# Revit family: PRD_AR_TltRllHldrs_STRATOSJumboRollHolder_STRX670
name_source: partatom
category: Specialty Equipment
revit_build: Autodesk Revit 2018 (Build: 20190510_1515(x64)
units: mm (PartAtom-declared; Revit-internal decimal feet)

## family parameters
Cut with Voids When Loaded = No
Host = Face
OmniClass Number = 23.40.20.21.17
OmniClass Title = Paper Towel Dispensers, Disposal Units
Part Type = Normal
Room Calculation Point = No
Round Connector Dimension = Use Diameter
Shared = No

## types (1)
- STRX670
    AssetType = Fixed
    BIMObjectName = PRD_AR_ToiletRollHolders_STRATOSJumboRollHolder_STRX670
    Category = Pr_40_20_76_88, Toilet roll holders
    Default Elevation = 850 mm  [stored 2.78871 ft]
    Description = Jumbo roll holder for wall mounting, stainless steel, surface satin finished, front with InoxPlus surface refinement for the reduction of finger marks and better cleaning characteristics (easy to clean), material thickness 1.5 mm, closed casing with curved front, paper withdrawal over two tear-off edges, cylinder lock with KWC standard key, for 1 roll with max. Ø 295 mm, includes stainless steel screws and dowels.
    DurationUnit = year
    Features = stainless steel, surface satin finished
    FillingQuantity = 1
    FillingQuantityUom = Rolls
    Finish = satin finished
    GrossWeight = 5.06 kg
    IfcExportAs = IfcFurnitureType
    IfcExportType = USERDEFINED
    IntegralAccessories = incl. stainless steel screws and dowels
    IsBuiltIn = TRUE
    Lock = Key-lock
    MainColor = stainless steel
    Manufacturer = KWC Group AG
    ManufacturerName = KWC Group AG
    ManufacturerURL = www.kwc.com
    Material = stainless steel
    MaterialCode = 1.4301
    MaterialThickness = 1.50 mm
    MaximumDepthDiameterOfConsumable = 295.00 mm
    MaximumWidthOfConsumable = 105.00 mm
    Model = STRX670
    ModelNumber = 2000057394
    ModelReference = STRX670
    NBSDescription = Toilet roll holders
    NBSReference = 45-35-72/368
    Name = Jumbo roll holder STRX670
    NetWeight = 4.37 kg
    NominalDepth = 170 mm  [stored 0.557743 ft]
    NominalHeight = 355 mm
    NominalWidth = 304 mm  [stored 0.997375 ft]
    ProductInformation = https://pim.kwc.com
    RollHolderMaterial = PRD_AR_StainlessSteel_SatinFinished
    Size = 304 x 355 x 170 mm
    Spindle = Yes
    Style = roll holder
    SurfaceTreatment = InoxPlus (anti fingerprint)
    TypeOfFixing = Screw
    TypeOfMounting = Wall mounting
    URL = www.kwc.com
    Uniclass2015Code = Pr_40_20_76_88
    Uniclass2015Title = Toilet roll holders
    Uniclass2015Version = Products v1.10
    Version = 1
    WarrantyDurationUnit = year

note: [stored X ft] marks values corroborated as IEEE doubles in the binary element streams (Revit-internal decimal feet)

## geometry (parser evidence)
native form markers: Sweep x6
no freeform markers — native parametric forms only
